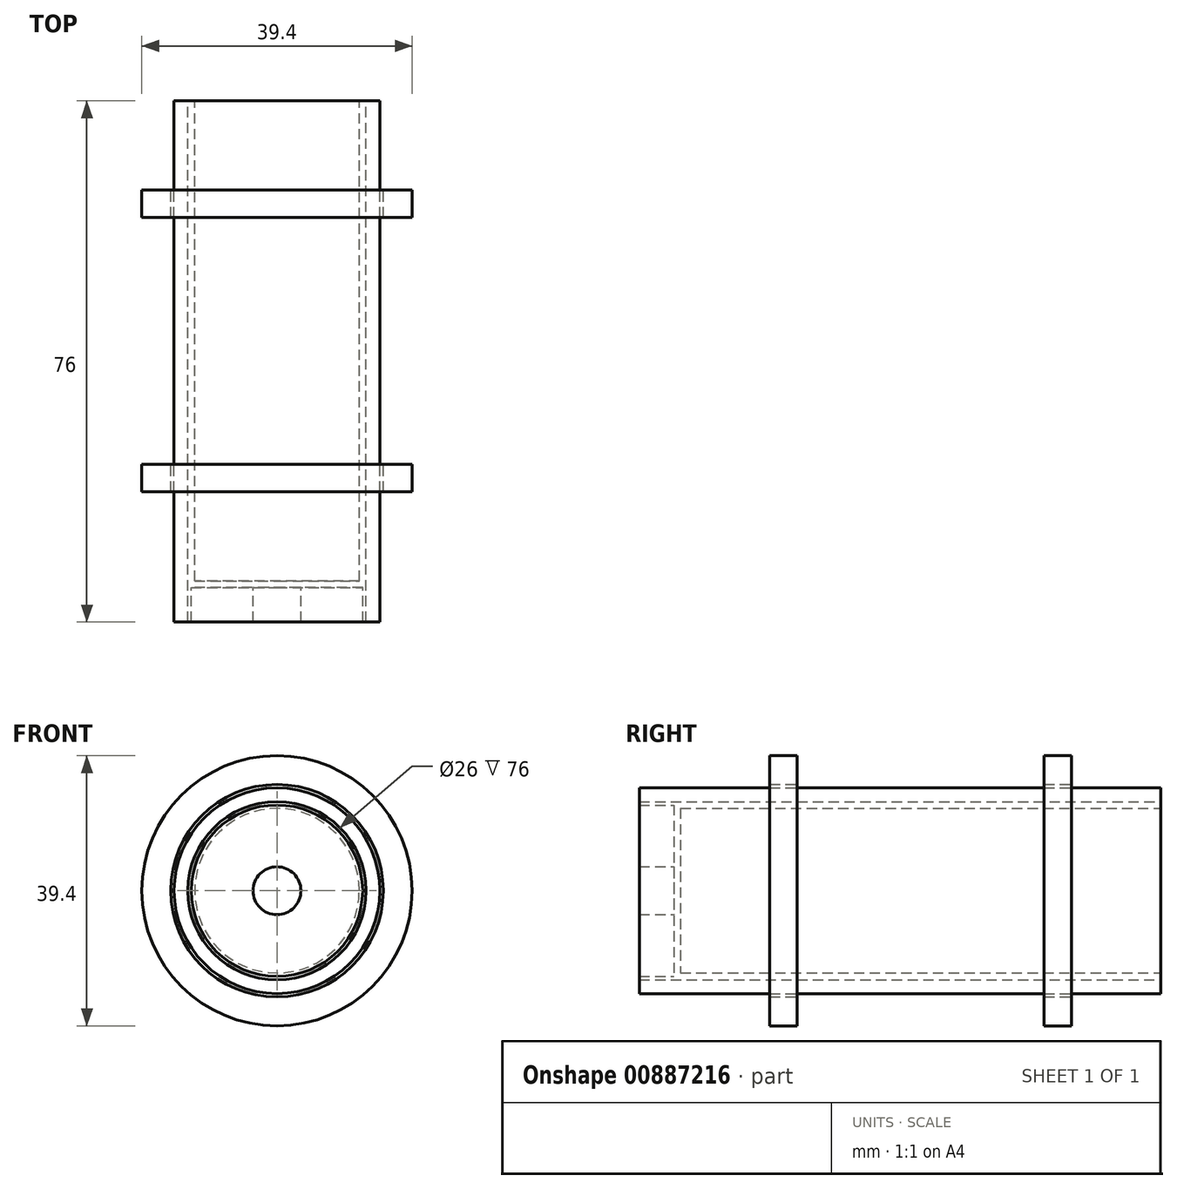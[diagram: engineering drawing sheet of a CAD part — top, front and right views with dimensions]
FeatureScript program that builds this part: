
annotation { "Feature Type Name" : "Feature", "Feature Type Description" : "" }
export const myFeature = defineFeature(function(context is Context, id is Id, definition is map)
    precondition{}
    {
        {
            var Q0;
            Q0=qCreatedBy(makeId("Right.planeOp"),FACE);
            var sketch = newSketch(context, id + "F0", { "sketchPlane" : qUnion([Q0])});
            skLineSegment(sketch, "E0.bottom", {"start": v(35, 0) * mm, "end": v(-35, 0) * mm});
            skLineSegment(sketch, "E0.top", {"start": v(35, -12) * mm, "end": v(-35, -12) * mm});
            skLineSegment(sketch, "E0.left", {"start": v(35, 0) * mm, "end": v(35, -12) * mm});
            skLineSegment(sketch, "E0.right", {"start": v(-35, 0) * mm, "end": v(-35, -12) * mm});
            skPoint(sketch, "E0.middle", {"position": v(0, -6) * mm});
            skSolve(sketch);
        }
        {
            var Q0;
            Q0=makeQuery(id+"F0.imprint","IMPRINT",FACE,{"disambiguationData":[TD([[makeQuery(id+"F0.imprint","IMPRINT",EDGE,{"derivedFrom":sQuery(id+"F0.wireOp",EDGE,"E0.bottom")}),1.0]])]});
            var Q1;
            Q1=sQuery(id+"F0.wireOp",EDGE,"E0.bottom");
            revolve(context, id + "F1", {"entities" : qUnion([Q0]), "axis" : qUnion([Q1]), "revolveType" : RevolveType.FULL});
        }
        {
            var Q0;
            Q0=qCreatedBy(makeId("Right.planeOp"),FACE);
            var sketch = newSketch(context, id + "F2", { "sketchPlane" : qUnion([Q0])});
            skLineSegment(sketch, "E1.bottom", {"start": v(35, -13) * mm, "end": v(-41, -13) * mm});
            skLineSegment(sketch, "E1.top", {"start": v(35, -15) * mm, "end": v(-41, -15) * mm});
            skLineSegment(sketch, "E1.left", {"start": v(35, -13) * mm, "end": v(35, -15) * mm});
            skLineSegment(sketch, "E1.right", {"start": v(-41, -13) * mm, "end": v(-41, -15) * mm});
            skPoint(sketch, "E1.middle", {"position": v(-3, -14) * mm});
            skLineSegment(sketch, "E2", {"start": v(51.51, 0) * mm, "end": v(-46.56, 0) * mm});
            skSolve(sketch);
        }
        {
            var Q0;
            Q0 = qSketchRegion(id + "F2", true);
            var Q1;
            Q1=sQuery(id+"F2.wireOp",EDGE,"E2");
            revolve(context, id + "F3", {"surfaceOperationType" : NewSurfaceOperationType.NEW, "entities" : qUnion([Q0]), "axis" : qUnion([Q1]), "revolveType" : RevolveType.FULL});
        }
        {
            var Q0;
            Q0=qCreatedBy(makeId("Right.planeOp"),FACE);
            var sketch = newSketch(context, id + "F4", { "sketchPlane" : qUnion([Q0])});
            skLineSegment(sketch, "E3.bottom", {"start": v(-22, -15.5) * mm, "end": v(-18, -15.5) * mm});
            skLineSegment(sketch, "E3.top", {"start": v(-22, -19.7) * mm, "end": v(-18, -19.7) * mm});
            skLineSegment(sketch, "E3.left", {"start": v(-22, -15.5) * mm, "end": v(-22, -19.7) * mm});
            skLineSegment(sketch, "E3.right", {"start": v(22, -15.5) * mm, "end": v(22, -19.7) * mm});
            skPoint(sketch, "E3.middle", {"position": v(0, -17.6) * mm});
            skLineSegment(sketch, "E4.left", {"start": v(-18, -15.5) * mm, "end": v(-18, -19.7) * mm});
            skLineSegment(sketch, "E4.right", {"start": v(18, -15.5) * mm, "end": v(18, -19.7) * mm});
            skLineSegment(sketch, "E5.trimOffspring", {"start": v(18, -19.7) * mm, "end": v(22, -19.7) * mm});
            skLineSegment(sketch, "E6.trimOffspring", {"start": v(18, -15.5) * mm, "end": v(22, -15.5) * mm});
            skSolve(sketch);
        }
        {
            var Q0;
            Q0 = qSketchRegion(id + "F4", true);
            var Q1;
            Q1=sQuery(id+"F2.wireOp",EDGE,"E2");
            revolve(context, id + "F5", {"surfaceOperationType" : NewSurfaceOperationType.NEW, "entities" : qUnion([Q0]), "axis" : qUnion([Q1]), "revolveType" : RevolveType.FULL});
        }
        {
            var Q0;
            Q0=qCreatedBy(makeId("Right.planeOp"),FACE);
            var sketch = newSketch(context, id + "F6", { "sketchPlane" : qUnion([Q0])});
            skLineSegment(sketch, "E7.bottom", {"start": v(-36, -3.5) * mm, "end": v(-41, -3.5) * mm});
            skLineSegment(sketch, "E7.top", {"start": v(-36, -12.5) * mm, "end": v(-41, -12.5) * mm});
            skLineSegment(sketch, "E7.left", {"start": v(-36, -3.5) * mm, "end": v(-36, -12.5) * mm});
            skLineSegment(sketch, "E7.right", {"start": v(-41, -3.5) * mm, "end": v(-41, -12.5) * mm});
            skPoint(sketch, "E7.middle", {"position": v(-38.5, -8) * mm});
            skSolve(sketch);
        }
        {
            var Q0;
            Q0 = qSketchRegion(id + "F6", true);
            var Q1;
            Q1=sQuery(id+"F2.wireOp",EDGE,"E2");
            revolve(context, id + "F7", {"surfaceOperationType" : NewSurfaceOperationType.NEW, "entities" : qUnion([Q0]), "axis" : qUnion([Q1]), "revolveType" : RevolveType.FULL});
        }
    });
